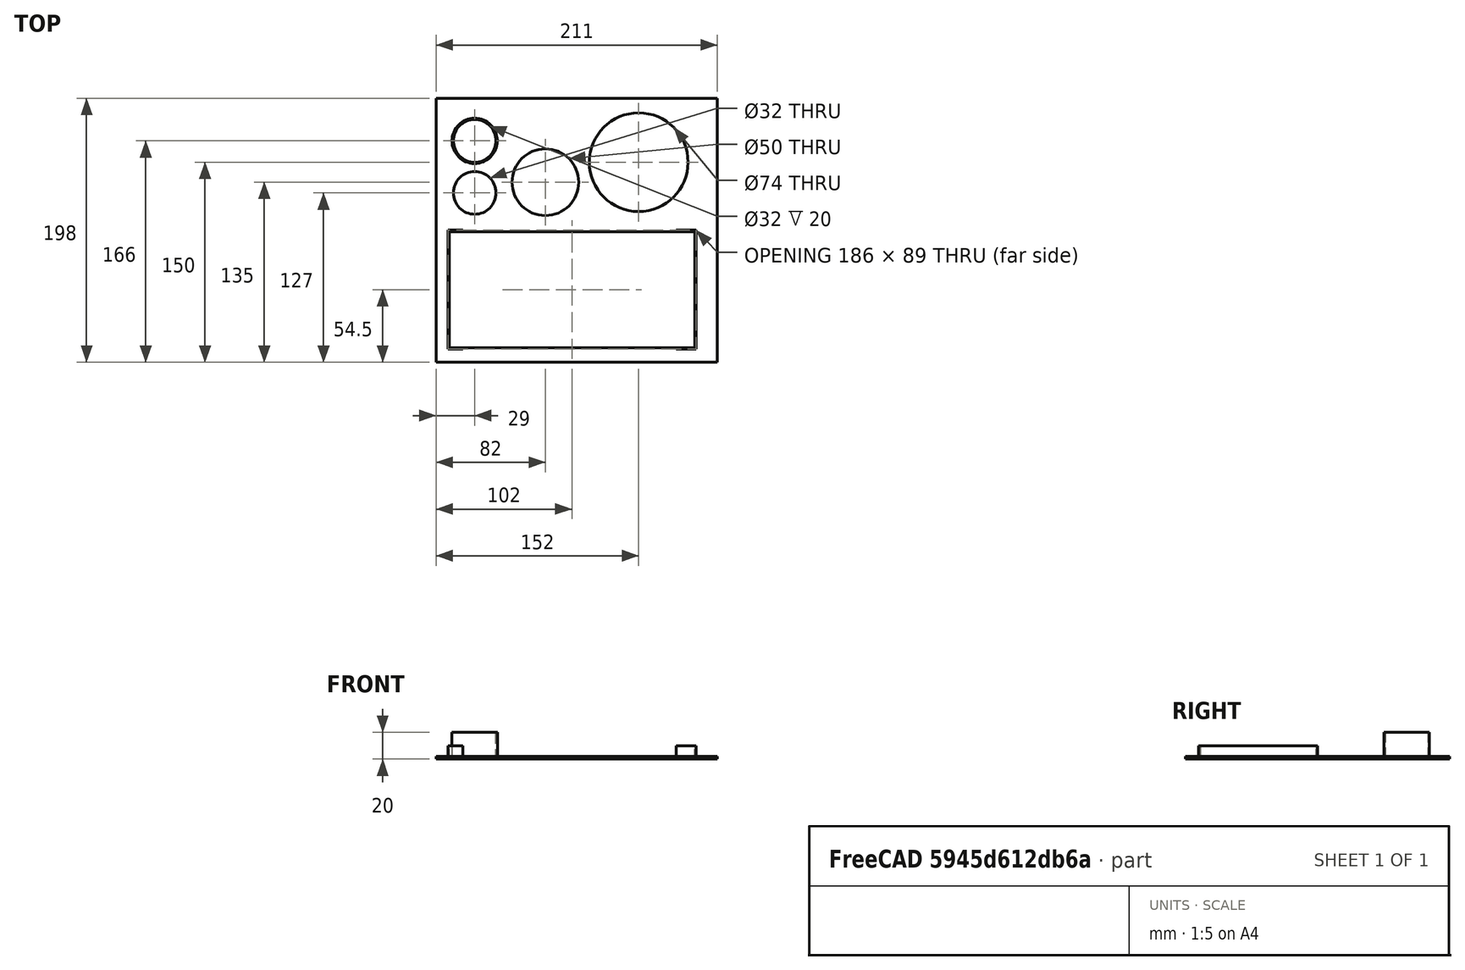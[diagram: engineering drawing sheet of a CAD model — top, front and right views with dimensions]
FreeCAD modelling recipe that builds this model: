
FCSTD DOCUMENT  (FreeCAD 0.20R29603 (Git))
Label: template
License: All rights reserved
LicenseURL: http://en.wikipedia.org/wiki/All_rights_reserved
objects: PartDesign::SubtractiveCylinder×4, PartDesign::AdditiveBox×2, PartDesign::SubtractiveBox×2, PartDesign::AdditiveCylinder×1, PartDesign::Body×1
note: 19 computed .brp shape members not serialized (recipe doc carries the construction recipe); baked Part::Feature solids carry a one-line shape summary decoded from their .brp

FEATURE [PartDesign::AdditiveBox] Box
  AttacherType = Attacher::AttachEngine3D
  Height = 2
  Length = 211
  MapMode = 5
  Support = -> [XY_Plane]
  Width = 198
  expr: Length = 211mm
FEATURE [PartDesign::AdditiveBox] Box001
  AttacherType = Attacher::AttachEngine3D
  AttachmentOffset = pos=(9,10,-2) rot=(0,0,1;0rad)
  BaseFeature = -> Box
  Height = 10
  Length = 186
  MapMode = 5
  Placement = pos=(9,10,0) rot=(0,0,1;0rad)
  Support = -> [Box]
  Width = 89
FEATURE [PartDesign::SubtractiveBox] Box002
  AttacherType = Attacher::AttachEngine3D
  AttachmentOffset = pos=(1,1,-2) rot=(0,0,1;0rad)
  BaseFeature = -> Box001
  Height = 10
  Length = 184
  MapMode = 5
  Placement = pos=(10,11,0) rot=(0,0,1;0rad)
  Support = -> [Box001]
  Width = 87
FEATURE [PartDesign::SubtractiveBox] Box003
  AttacherType = Attacher::AttachEngine3D
  AttachmentOffset = pos=(10,-1,0) rot=(0,0,1;0rad)
  BaseFeature = -> Box002
  Height = 10
  Length = 160
  MapMode = 5
  Placement = pos=(20,10,2) rot=(0,0,1;0rad)
  Support = -> [Box002]
  Width = 89
FEATURE [PartDesign::SubtractiveCylinder] Cylinder
  Angle = 360
  AttacherType = Attacher::AttachEngine3D
  AttachmentOffset = pos=(29,127,0) rot=(0,0,1;0rad)
  BaseFeature = -> Box003
  FirstAngle = 0
  Height = 2
  MapMode = 5
  Placement = pos=(29,127,0) rot=(0,0,1;0rad)
  Radius = 16
  SecondAngle = 0
  Support = -> [XY_Plane]
FEATURE [PartDesign::SubtractiveCylinder] Cylinder001
  Angle = 360
  AttacherType = Attacher::AttachEngine3D
  AttachmentOffset = pos=(82,135,0) rot=(0,0,1;0rad)
  BaseFeature = -> Cylinder
  FirstAngle = 0
  Height = 2
  MapMode = 5
  Placement = pos=(82,135,0) rot=(0,0,1;0rad)
  Radius = 25
  SecondAngle = 0
  Support = -> [XY_Plane]
FEATURE [PartDesign::AdditiveCylinder] Cylinder002
  Angle = 360
  AttacherType = Attacher::AttachEngine3D
  AttachmentOffset = pos=(29,166,0) rot=(0,0,1;0rad)
  BaseFeature = -> Cylinder001
  FirstAngle = 0
  Height = 20
  MapMode = 5
  Placement = pos=(29,166,0) rot=(0,0,1;0rad)
  Radius = 17
  SecondAngle = 0
  Support = -> [XY_Plane]
FEATURE [PartDesign::SubtractiveCylinder] Cylinder003
  Angle = 360
  AttacherType = Attacher::AttachEngine3D
  BaseFeature = -> Cylinder002
  FirstAngle = 0
  Height = 20
  MapMode = 2
  Placement = pos=(29,166,0) rot=(0,0,1;0rad)
  Radius = 16
  SecondAngle = 0
  Support = -> [Cylinder002]
FEATURE [PartDesign::SubtractiveCylinder] Cylinder004
  Angle = 360
  AttacherType = Attacher::AttachEngine3D
  AttachmentOffset = pos=(152,150,0) rot=(0,0,1;0rad)
  BaseFeature = -> Cylinder003
  FirstAngle = 0
  Height = 2
  MapMode = 5
  Placement = pos=(152,150,0) rot=(0,0,1;0rad)
  Radius = 37
  SecondAngle = 0
  Support = -> [XY_Plane]
FEATURE [PartDesign::Body] Body
  Group = -> [Box,Box001,Box002,Box003,Cylinder,Cylinder001,Cylinder002,Cylinder003,Cylinder004]
  Origin = -> Origin
  Tip = -> Cylinder004
